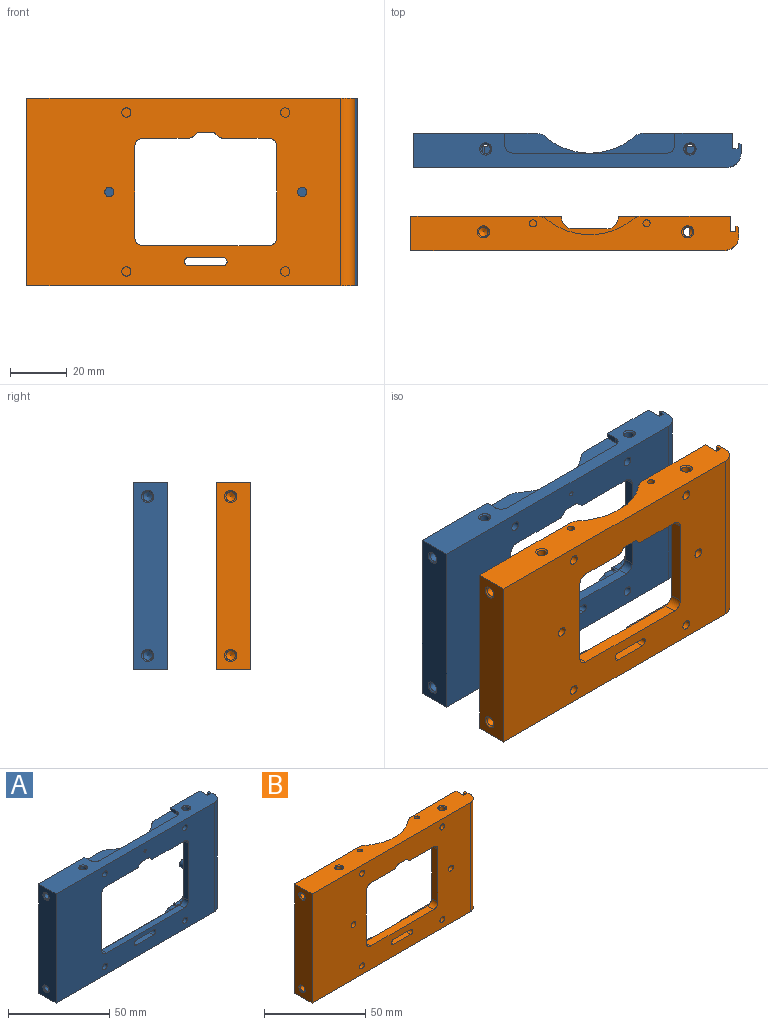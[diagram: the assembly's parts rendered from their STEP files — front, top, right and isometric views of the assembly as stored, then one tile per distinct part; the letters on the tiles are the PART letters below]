
ASSEMBLY  parts=2 mates=1
PART A: 129 faces, bbox 115.5x12x66 mm
  f0: plane 66x43.31mm, normal (0,1,0), area 1725.1mm2, adj f1,f11,f34,f40,f41,f42,f76,f77
  f1: plane 115.5x12mm, normal (0,0,-1), area 945mm2, adj f0,f4,f5,f12,f14,f39,f41,f45
  f2: cylinder r=1.65mm len=10mm, axis (0,1,0), area 103.7mm2, adj f45,f125
  f3: cylinder r=1.65mm len=10mm, axis (0,1,0), area 103.7mm2, adj f45,f128
  f4: plane 7x5.5mm, normal (1,0,0), area 38.5mm2, adj f1,f8,f12,f128
  f5: plane 7x5.5mm, normal (-1,0,0), area 38.5mm2, adj f1,f9,f12,f125
  f6: cylinder r=3.5mm len=5.5mm, axis (0,-1,0), area 23.6mm2, adj f9,f10,f12,f125
  f7: cylinder r=3.5mm len=5.5mm, axis (0,-1,0), area 23.6mm2, adj f8,f12,f117,f128
  f8: cylinder r=5mm len=5.5mm, axis (0,1,0), area 11.8mm2, adj f4,f7,f12,f128
  f9: cylinder r=5mm len=5.5mm, axis (0,1,0), area 11.8mm2, adj f5,f6,f12,f125
  f10: cylinder r=5mm len=7.5mm, axis (0,-1,0), area 18.2mm2, adj f6,f12,f14,f78,f125,f126
  f11: plane 7.5x3.18mm, normal (0,0,1), area 21.8mm2, adj f0,f12,f52,f79,f117
  f12: plane 78x56.5mm, normal (0,1,0), area 1402.9mm2, adj f1,f4,f5,f6,f7,f8,f9,f10
  f13: plane 43.5x7.5mm, normal (-1,0,0), area 302.3mm2, adj f12,f14,f83,f84,f85,f89,f90
  f14: plane 66x31.41mm, normal (0,1,0), area 939.7mm2, adj f1,f10,f13,f33,f40,f43,f47,f74
  f15: plane 54.5x3.5mm, normal (0,0,1), area 190.7mm2, adj f28,f29,f45,f109
  f16: cylinder r=3mm len=3.5mm, axis (0,1,0), area 16.5mm2, adj f17,f30,f45,f115
  f17: plane 21.75x3.5mm, normal (0,0,-1), area 76.1mm2, adj f16,f18,f45,f116
  f18: cylinder r=1mm len=3.5mm, axis (0,1,0), area 2.6mm2, adj f17,f19,f45,f114
  f19: plane 3.5x1.63mm, normal (0.68,0,-0.73), area 7.8mm2, adj f18,f20,f45,f112
  f20: cylinder r=1.75mm len=3.5mm, axis (0,1,0), area 4.6mm2, adj f19,f21,f45,f110
  f21: plane 4x3.5mm, normal (0,0,-1), area 14mm2, adj f20,f22,f45,f108
  f22: cylinder r=1.75mm len=3.5mm, axis (0,1,0), area 4.6mm2, adj f21,f23,f45,f106
  f23: plane 3.5x1.63mm, normal (-0.68,0,-0.73), area 7.8mm2, adj f22,f24,f45,f104
  f24: cylinder r=1mm len=3.5mm, axis (0,1,0), area 2.6mm2, adj f23,f25,f45,f102
  f25: plane 21.75x3.5mm, normal (0,0,-1), area 76.1mm2, adj f24,f26,f45,f101
  f26: cylinder r=3mm len=3.5mm, axis (0,1,0), area 16.5mm2, adj f25,f27,f45,f103
  f27: plane 34.5x3.5mm, normal (-1,0,0), area 120.8mm2, adj f26,f28,f45,f105
  f28: cylinder r=3mm len=3.5mm, axis (0,1,0), area 16.5mm2, adj f15,f27,f45,f107
  f29: cylinder r=3mm len=3.5mm, axis (0,1,0), area 16.5mm2, adj f15,f30,f45,f111
  f30: plane 34.5x3.5mm, normal (1,0,0), area 120.8mm2, adj f16,f29,f45,f113
  f31: cylinder r=1.65mm len=9.15mm, axis (0,0,1), area 93.6mm2, adj f59,f82,f83
  f32: cylinder r=24mm len=31.27mm, axis (0,0,1), area 253.4mm2, adj f33,f34,f44,f82,f121,f124
  f33: cylinder r=5mm len=7.5mm, axis (0,0,1), area 26.6mm2, adj f14,f32,f82,f121
  f34: cylinder r=5mm len=7.5mm, axis (0,0,1), area 26.6mm2, adj f0,f32,f82,f124
  f35: cylinder r=1.5mm len=4.5mm, axis (0,1,0), area 21.2mm2, adj f12,f36,f38,f45
  f36: plane 12x4.5mm, normal (0,0,-1), area 54mm2, adj f12,f35,f37,f45
  f37: cylinder r=1.5mm len=4.5mm, axis (0,1,0), area 21.2mm2, adj f12,f36,f38,f45
  f38: plane 12x4.5mm, normal (0,0,1), area 54mm2, adj f12,f35,f37,f45
  f39: plane 66x3mm, normal (1,0,0), area 198mm2, adj f1,f40,f46,f51
  f40: plane 115.5x12mm, normal (0,0,1), area 920.8mm2, adj f0,f14,f39,f41,f45,f46,f47,f48
  f41: plane 66x12mm, normal (-1,0,0), area 763mm2, adj f0,f1,f40,f45,f64,f65
  f42: cylinder r=1.65mm len=12mm, axis (0,1,0), area 124.4mm2, adj f0,f45
  f43: cylinder r=1.65mm len=12mm, axis (0,1,0), area 124.4mm2, adj f14,f45
  f44: cylinder r=0.8mm len=5mm, axis (0,1,0), area 25.1mm2, adj f32,f45
  f45: plane 110.5x66mm, normal (0,-1,0), area 4753.7mm2, adj f1,f2,f3,f15,f16,f17,f18,f19
  f46: cylinder r=5mm len=66mm, axis (0,0,-1), area 518.4mm2, adj f1,f39,f40,f45
  f47: plane 66x5.5mm, normal (1,0,0), area 363mm2, adj f1,f14,f40,f48
  f48: plane 66x2mm, normal (0,1,0), area 132mm2, adj f1,f40,f47,f49
  f49: plane 66x2mm, normal (-1,0,0), area 132mm2, adj f1,f40,f48,f50
  f50: plane 66x0.5mm, normal (0,1,0), area 33mm2, adj f1,f40,f49,f51
  f51: plane 66x0.5mm, normal (0.71,0.71,0), area 46.7mm2, adj f1,f39,f40,f50
  f52: cylinder r=1.65mm len=7.64mm, axis (0,0,-1), area 70.8mm2, adj f11,f55,f79
  f53: cylinder r=1.65mm len=6.65mm, axis (0,0,-1), area 67.7mm2, adj f54,f78,f84
  f54: cone r=1.65mm half-angle=45deg, axis (0,0,-1), area 8.4mm2, adj f1,f53
  f55: cone r=1.65mm half-angle=45deg, axis (0,0,-1), area 8.4mm2, adj f1,f52
  f56: cone r=0mm half-angle=59deg, axis (0,0,1), area 0.9mm2, adj f57,f81
  f57: cylinder r=1.65mm len=9.5mm, axis (0,0,1), area 95.5mm2, adj f56,f58,f81,f82
  f58: cone r=1.65mm half-angle=45deg, axis (0,0,1), area 8.4mm2, adj f40,f57
  f59: cone r=1.65mm half-angle=45deg, axis (0,0,1), area 8.4mm2, adj f31,f40
  f60: cone r=0mm half-angle=59deg, axis (-1,0,0), area 10mm2, adj f61
  f61: cylinder r=1.65mm len=9.5mm, axis (-1,0,0), area 98.5mm2, adj f60,f65
  f62: cone r=0mm half-angle=59deg, axis (-1,0,0), area 10mm2, adj f63
  f63: cylinder r=1.65mm len=9.5mm, axis (-1,0,0), area 98.5mm2, adj f62,f64
  f64: cone r=1.65mm half-angle=45deg, axis (-1,0,0), area 8.4mm2, adj f41,f63
  f65: cone r=1.65mm half-angle=45deg, axis (-1,0,0), area 8.4mm2, adj f41,f61
  f66: cone r=0mm half-angle=59deg, axis (0,1,0), area 5.7mm2, adj f67
  f67: cylinder r=1.25mm len=7.5mm, axis (0,1,0), area 58.9mm2, adj f66,f77
  f68: cone r=0mm half-angle=59deg, axis (0,1,0), area 5.7mm2, adj f69
  f69: cylinder r=1.25mm len=7.5mm, axis (0,1,0), area 58.9mm2, adj f68,f76
  f70: cone r=0mm half-angle=59deg, axis (0,1,0), area 5.7mm2, adj f71
  f71: cylinder r=1.25mm len=7.5mm, axis (0,1,0), area 58.9mm2, adj f70,f75
  f72: cone r=0mm half-angle=59deg, axis (0,1,0), area 5.7mm2, adj f73
  f73: cylinder r=1.25mm len=7.5mm, axis (0,1,0), area 58.9mm2, adj f72,f74
  f74: cone r=1.25mm half-angle=45deg, axis (0,1,0), area 6.7mm2, adj f14,f73
  f75: cone r=1.25mm half-angle=45deg, axis (0,1,0), area 6.7mm2, adj f14,f71
  f76: cone r=1.25mm half-angle=45deg, axis (0,1,0), area 6.7mm2, adj f0,f69
  f77: cone r=1.25mm half-angle=45deg, axis (0,1,0), area 6.7mm2, adj f0,f67
  f78: plane 7.5x3.18mm, normal (0,0,1), area 17.3mm2, adj f10,f12,f14,f53,f84
  f79: cylinder r=3mm len=7.5mm, axis (0,1,0), area 28.1mm2, adj f0,f11,f12,f52,f80
  f80: plane 43.5x7.5mm, normal (1,0,0), area 302.3mm2, adj f0,f12,f79,f81,f92,f93,f96
  f81: cylinder r=3mm len=7.5mm, axis (0,1,0), area 29.1mm2, adj f0,f12,f56,f57,f80,f82
  f82: plane 72x7.5mm, normal (0,0,-1), area 367.2mm2, adj f0,f12,f14,f31,f32,f33,f34,f57
  f83: cylinder r=3mm len=7.5mm, axis (0,1,0), area 33.3mm2, adj f12,f13,f14,f31,f82
  f84: cylinder r=3mm len=7.5mm, axis (0,1,0), area 33.3mm2, adj f12,f13,f14,f53,f78
  f85: cylinder r=2mm len=3mm, axis (0,-1,0), area 9.4mm2, adj f12,f13,f86,f90
  f86: plane 3x3mm, normal (0,0,-1), area 9mm2, adj f12,f85,f87,f90
  f87: cylinder r=2.38mm len=4.75mm, axis (0,-1,0), area 22.4mm2, adj f12,f86,f88,f90
  f88: plane 3x2.99mm, normal (0,0,1), area 9mm2, adj f12,f87,f89,f90
  f89: cylinder r=2.25mm len=3mm, axis (0,-1,0), area 7.5mm2, adj f12,f13,f88,f90
  f90: plane 8x7.38mm, normal (0,1,0), area 29.3mm2, adj f13,f85,f86,f87,f88,f89,f100
  f91: plane 3x3mm, normal (0,0,-1), area 9mm2, adj f12,f92,f95,f96
  f92: cylinder r=2mm len=3mm, axis (0,-1,0), area 9.4mm2, adj f12,f80,f91,f96
  f93: cylinder r=2.25mm len=3mm, axis (0,-1,0), area 7.5mm2, adj f12,f80,f94,f96
  f94: plane 3x2.99mm, normal (0,0,1), area 9mm2, adj f12,f93,f95,f96
  f95: cylinder r=2.38mm len=4.75mm, axis (0,-1,0), area 22.4mm2, adj f12,f91,f94,f96
  f96: plane 8x7.38mm, normal (0,1,0), area 29.3mm2, adj f80,f91,f92,f93,f94,f95,f98
  f97: cone r=0mm half-angle=59deg, axis (0,1,0), area 5.7mm2, adj f98
  f98: cylinder r=1.25mm len=6mm, axis (0,1,0), area 47.1mm2, adj f96,f97
  f99: cone r=0mm half-angle=59deg, axis (0,1,0), area 5.7mm2, adj f100
  f100: cylinder r=1.25mm len=6mm, axis (0,1,0), area 47.1mm2, adj f90,f99
  f101: plane 21.75x1mm, normal (0,0.71,-0.71), area 30.8mm2, adj f12,f25,f102,f103
  f102: cone r=1mm half-angle=45deg, axis (0,-1,0), area 0.5mm2, adj f24,f101,f104
  f103: cone r=3mm half-angle=45deg, axis (0,1,0), area 7.8mm2, adj f12,f26,f101,f105
  f104: plane 2.31x2.25mm, normal (-0.48,0.71,-0.52), area 3.1mm2, adj f12,f23,f102,f106
  f105: plane 34.5x1mm, normal (-0.71,0.71,0), area 48.8mm2, adj f12,f27,f103,f107
  f106: cone r=1.75mm half-angle=45deg, axis (0,1,0), area 2.4mm2, adj f12,f22,f104,f108
  f107: cone r=3mm half-angle=45deg, axis (0,1,0), area 7.8mm2, adj f12,f28,f105,f109
  f108: plane 4x1mm, normal (0,0.71,-0.71), area 5.7mm2, adj f21,f82,f106,f110
  f109: plane 54.5x1mm, normal (0,0.71,0.71), area 77.1mm2, adj f12,f15,f107,f111
  f110: cone r=2.75mm half-angle=45deg, axis (0,1,0), area 2.4mm2, adj f12,f20,f108,f112
  f111: cone r=3mm half-angle=45deg, axis (0,1,0), area 7.8mm2, adj f12,f29,f109,f113
  f112: plane 2.31x2.25mm, normal (0.48,0.71,-0.52), area 3.1mm2, adj f12,f19,f110,f114
  f113: plane 34.5x1mm, normal (0.71,0.71,0), area 48.8mm2, adj f12,f30,f111,f115
  f114: cone r=1mm half-angle=45deg, axis (0,-1,0), area 0.5mm2, adj f18,f112,f116
  f115: cone r=3mm half-angle=45deg, axis (0,1,0), area 7.8mm2, adj f12,f16,f113,f116
  f116: plane 21.75x1mm, normal (0,0.71,-0.71), area 30.8mm2, adj f12,f17,f114,f115
  f117: cylinder r=5mm len=7.5mm, axis (0,-1,0), area 18.2mm2, adj f0,f7,f11,f12,f127,f128
  f118: plane 54x2mm, normal (0,1,0), area 108mm2, adj f40,f119,f121,f123,f124
  f119: cylinder r=3mm len=3mm, axis (0,0,1), area 9.4mm2, adj f40,f118,f120,f121
  f120: plane 4x2mm, normal (-1,0,0), area 8mm2, adj f14,f40,f119,f121
  f121: plane 30x7mm, normal (0,0,1), area 125.9mm2, adj f14,f32,f33,f118,f119,f120
  f122: plane 4x2mm, normal (1,0,0), area 8mm2, adj f0,f40,f123,f124
  f123: cylinder r=3mm len=3mm, axis (0,0,1), area 9.4mm2, adj f40,f118,f122,f124
  f124: plane 30x7mm, normal (0,0,1), area 125.9mm2, adj f0,f32,f34,f118,f122,f123
  f125: plane 8.5x8mm, normal (0,1,0), area 54.1mm2, adj f1,f2,f5,f6,f9,f10,f126
  f126: plane 7.07x2mm, normal (-1,0,0), area 14.1mm2, adj f1,f10,f14,f125
  f127: plane 7.07x2mm, normal (1,0,0), area 14.1mm2, adj f0,f1,f117,f128
  f128: plane 8.5x8mm, normal (0,1,0), area 54.1mm2, adj f1,f3,f4,f7,f8,f117,f127
PART B: 99 faces, bbox 115.5x12x66 mm
  f0: plane 16.17x4.5mm, normal (0,0,-1), area 72.8mm2, adj f1,f8,f28,f92
  f1: plane 110.5x66mm, normal (0,-1,0), area 5290.3mm2, adj f0,f3,f4,f12,f13,f14,f16,f17
  f2: plane 66x53mm, normal (0,1,0), area 1897.5mm2, adj f3,f4,f9,f10,f21,f37,f44,f45
  f3: plane 70x12mm, normal (0,0,1), area 494mm2, adj f1,f2,f5,f6,f8,f12,f14,f50
  f4: plane 115.5x12mm, normal (0,0,1), area 1179.7mm2, adj f1,f2,f5,f11,f15,f31,f32,f33
  f5: plane 66x39.5mm, normal (0,1,0), area 1006.5mm2, adj f3,f4,f6,f7,f21,f32,f39,f40
  f6: plane 7.5x6mm, normal (-1,0,0), area 34.3mm2, adj f3,f5,f8,f41,f60,f61
  f7: plane 7.5x6mm, normal (-1,0,0), area 34.3mm2, adj f5,f8,f39,f48,f54,f55
  f8: plane 80x52mm, normal (0,1,0), area 2057.8mm2, adj f0,f3,f6,f7,f9,f10,f12,f13
  f9: plane 7.5x1mm, normal (0,0,1), area 7.5mm2, adj f2,f8,f44,f50
  f10: plane 7.5x1mm, normal (0,0,-1), area 7.5mm2, adj f2,f8,f45,f49
  f11: plane 66x0.5mm, normal (0,1,0), area 33mm2, adj f4,f21,f34,f35
  f12: cylinder r=1.5mm len=4.5mm, axis (0,1,0), area 21.2mm2, adj f1,f3,f8,f13
  f13: plane 12x4.5mm, normal (0,0,-1), area 54mm2, adj f1,f8,f12,f14
  f14: cylinder r=1.5mm len=4.5mm, axis (0,1,0), area 21.2mm2, adj f1,f3,f8,f13
  f15: plane 66x3mm, normal (1,0,0), area 198mm2, adj f4,f21,f31,f35
  f16: plane 44x4.5mm, normal (0,0,1), area 198mm2, adj f1,f8,f27,f30
  f17: plane 32x4.5mm, normal (1,0,0), area 144mm2, adj f1,f8,f27,f28
  f18: plane 16.17x4.5mm, normal (0,0,-1), area 72.8mm2, adj f1,f8,f29,f98
  f19: cylinder r=1.65mm len=4.5mm, axis (0,1,0), area 46.7mm2, adj f1,f8
  f20: cylinder r=1.65mm len=4.5mm, axis (0,1,0), area 46.7mm2, adj f1,f8
  f21: plane 115.5x12mm, normal (0,0,-1), area 1257.8mm2, adj f1,f2,f5,f11,f15,f31,f32,f33
  f22: plane 32x4.5mm, normal (-1,0,0), area 144mm2, adj f1,f8,f29,f30
  f23: cylinder r=1.65mm len=4.5mm, axis (0,1,0), area 46.7mm2, adj f1,f36
  f24: cylinder r=1.65mm len=4.5mm, axis (0,1,0), area 46.7mm2, adj f1,f42
  f25: cylinder r=1.65mm len=4.5mm, axis (0,1,0), area 46.7mm2, adj f1,f43
  f26: cylinder r=1.65mm len=4.5mm, axis (0,1,0), area 46.7mm2, adj f1,f38
  f27: cylinder r=3mm len=4.5mm, axis (0,-1,0), area 21.2mm2, adj f1,f8,f16,f17
  f28: cylinder r=3mm len=4.5mm, axis (0,1,0), area 21.2mm2, adj f0,f1,f8,f17
  f29: cylinder r=3mm len=4.5mm, axis (0,-1,0), area 21.2mm2, adj f1,f8,f18,f22
  f30: cylinder r=3mm len=4.5mm, axis (0,1,0), area 21.2mm2, adj f1,f8,f16,f22
  f31: cylinder r=5mm len=66mm, axis (0,0,-1), area 518.4mm2, adj f1,f4,f15,f21
  f32: plane 66x5.5mm, normal (1,0,0), area 363mm2, adj f4,f5,f21,f33
  f33: plane 66x2mm, normal (0,1,0), area 132mm2, adj f4,f21,f32,f34
  f34: plane 66x2mm, normal (-1,0,0), area 132mm2, adj f4,f11,f21,f33
  f35: plane 66x0.5mm, normal (0.71,0.71,0), area 46.7mm2, adj f4,f11,f15,f21
  f36: plane 3.3x3.3mm, normal (0,-1,0), area 8.6mm2, adj f23
  f37: plane 32x7.5mm, normal (1,0,0), area 240mm2, adj f2,f8,f44,f45
  f38: plane 3.3x3.3mm, normal (0,-1,0), area 8.6mm2, adj f26
  f39: plane 7.5x1mm, normal (0,0,-1), area 7.5mm2, adj f5,f7,f8,f47
  f40: plane 32x7.5mm, normal (-1,0,0), area 240mm2, adj f5,f8,f46,f47
  f41: plane 7.5x1mm, normal (0,0,1), area 7.5mm2, adj f5,f6,f8,f46
  f42: plane 3.3x3.3mm, normal (0,-1,0), area 8.6mm2, adj f24
  f43: plane 3.3x3.3mm, normal (0,-1,0), area 8.6mm2, adj f25
  f44: cylinder r=4mm len=7.5mm, axis (0,-1,0), area 47.1mm2, adj f2,f8,f9,f37
  f45: cylinder r=4mm len=7.5mm, axis (0,-1,0), area 47.1mm2, adj f2,f8,f10,f37
  f46: cylinder r=4mm len=7.5mm, axis (0,-1,0), area 47.1mm2, adj f5,f8,f40,f41
  f47: cylinder r=4mm len=7.5mm, axis (0,-1,0), area 47.1mm2, adj f5,f8,f39,f40
  f48: plane 70x7.5mm, normal (0,0,-1), area 361.8mm2, adj f2,f5,f7,f8,f49,f51,f52,f53
  f49: plane 7.5x6mm, normal (1,0,0), area 45mm2, adj f2,f8,f10,f48
  f50: plane 7.5x6mm, normal (1,0,0), area 45mm2, adj f2,f3,f8,f9
  f51: cylinder r=24mm len=30.28mm, axis (0,0,1), area 229.4mm2, adj f4,f48,f66,f67
  f52: cylinder r=1.25mm len=7mm, axis (0,0,1), area 55mm2, adj f4,f48
  f53: cylinder r=1.25mm len=7mm, axis (0,0,1), area 55mm2, adj f4,f48
  f54: cone r=0mm half-angle=59deg, axis (0,0,1), area 3.1mm2, adj f7,f55
  f55: cylinder r=1.65mm len=9.5mm, axis (0,0,1), area 79.9mm2, adj f7,f48,f54,f59
  f56: cone r=0mm half-angle=59deg, axis (0,0,1), area 10mm2, adj f57
  f57: cylinder r=1.65mm len=9.5mm, axis (0,0,1), area 98.5mm2, adj f56,f58
  f58: cone r=1.65mm half-angle=45deg, axis (0,0,1), area 8.4mm2, adj f4,f57
  f59: cone r=1.65mm half-angle=45deg, axis (0,0,1), area 8.4mm2, adj f4,f55
  f60: cone r=0mm half-angle=59deg, axis (0,0,-1), area 3.1mm2, adj f6,f61
  f61: cylinder r=1.65mm len=9.5mm, axis (0,0,-1), area 79.9mm2, adj f3,f6,f60,f65
  f62: cone r=0mm half-angle=59deg, axis (0,0,-1), area 10mm2, adj f63
  f63: cylinder r=1.65mm len=9.5mm, axis (0,0,-1), area 98.5mm2, adj f62,f64
  f64: cone r=1.65mm half-angle=45deg, axis (0,0,-1), area 8.4mm2, adj f21,f63
  f65: cone r=1.65mm half-angle=45deg, axis (0,0,-1), area 8.4mm2, adj f21,f61
  f66: cylinder r=5mm len=7mm, axis (0,0,1), area 23.9mm2, adj f2,f4,f48,f51
  f67: cylinder r=5mm len=7mm, axis (0,0,1), area 23.9mm2, adj f4,f5,f48,f51
  f68: plane 66x12mm, normal (-1,0,0), area 763mm2, adj f1,f2,f4,f21,f73,f74
  f69: cone r=0mm half-angle=59deg, axis (-1,0,0), area 10mm2, adj f70
  f70: cylinder r=1.65mm len=9.5mm, axis (-1,0,0), area 98.5mm2, adj f69,f74
  f71: cone r=0mm half-angle=59deg, axis (-1,0,0), area 10mm2, adj f72
  f72: cylinder r=1.65mm len=9.5mm, axis (-1,0,0), area 98.5mm2, adj f71,f73
  f73: cone r=1.65mm half-angle=45deg, axis (-1,0,0), area 8.4mm2, adj f68,f72
  f74: cone r=1.65mm half-angle=45deg, axis (-1,0,0), area 8.4mm2, adj f68,f70
  f75: cone r=0mm half-angle=59deg, axis (0,1,0), area 19.4mm2, adj f76
  f76: cylinder r=2.3mm len=7.5mm, axis (0,1,0), area 108.4mm2, adj f75,f86
  f77: cone r=0mm half-angle=59deg, axis (0,1,0), area 19.4mm2, adj f78
  f78: cylinder r=2.3mm len=7.5mm, axis (0,1,0), area 108.4mm2, adj f77,f85
  f79: cone r=0mm half-angle=59deg, axis (0,1,0), area 19.4mm2, adj f80
  f80: cylinder r=2.3mm len=7.5mm, axis (0,1,0), area 108.4mm2, adj f79,f84
  f81: cone r=0mm half-angle=59deg, axis (0,1,0), area 19.4mm2, adj f82
  f82: cylinder r=2.3mm len=7.5mm, axis (0,1,0), area 108.4mm2, adj f81,f83
  f83: cone r=2.3mm half-angle=45deg, axis (0,1,0), area 11.3mm2, adj f5,f82
  f84: cone r=2.3mm half-angle=45deg, axis (0,1,0), area 11.3mm2, adj f5,f80
  f85: cone r=2.3mm half-angle=45deg, axis (0,1,0), area 11.3mm2, adj f2,f78
  f86: cone r=2.3mm half-angle=45deg, axis (0,1,0), area 11.3mm2, adj f2,f76
  f87: plane 7x0.3mm, normal (-1,0,0), area 2.1mm2, adj f3,f5,f21,f88
  f88: cylinder r=4mm len=7mm, axis (0,0,-1), area 44mm2, adj f3,f21,f87,f89
  f89: plane 12x7mm, normal (0,1,0), area 84mm2, adj f3,f21,f88,f90
  f90: cylinder r=4mm len=7mm, axis (0,0,-1), area 44mm2, adj f3,f21,f89,f91
  f91: plane 7x0.3mm, normal (1,0,0), area 2.1mm2, adj f2,f3,f21,f90
  f92: cylinder r=2mm len=4.5mm, axis (0,1,0), area 7.1mm2, adj f0,f1,f8,f93
  f93: plane 4.5x0.83mm, normal (0.71,0,-0.71), area 5.3mm2, adj f1,f8,f92,f94
  f94: cylinder r=2mm len=4.5mm, axis (0,1,0), area 7.1mm2, adj f1,f8,f93,f95
  f95: plane 4.5x4.34mm, normal (0,0,-1), area 19.5mm2, adj f1,f8,f94,f96
  f96: cylinder r=2mm len=4.5mm, axis (0,1,0), area 7.1mm2, adj f1,f8,f95,f97
  f97: plane 4.5x0.83mm, normal (-0.71,0,-0.71), area 5.3mm2, adj f1,f8,f96,f98
  f98: cylinder r=2mm len=4.5mm, axis (0,1,0), area 7.1mm2, adj f1,f8,f18,f97
PLACE A t=(13.14,30.89,-2.6)mm
PLACE B t=(13.14,-5.84,-2.6)mm
MATE planar B.f4 <-> A.f40  axis (0,0,1) through (6.14,-4.82,30.4)mm
